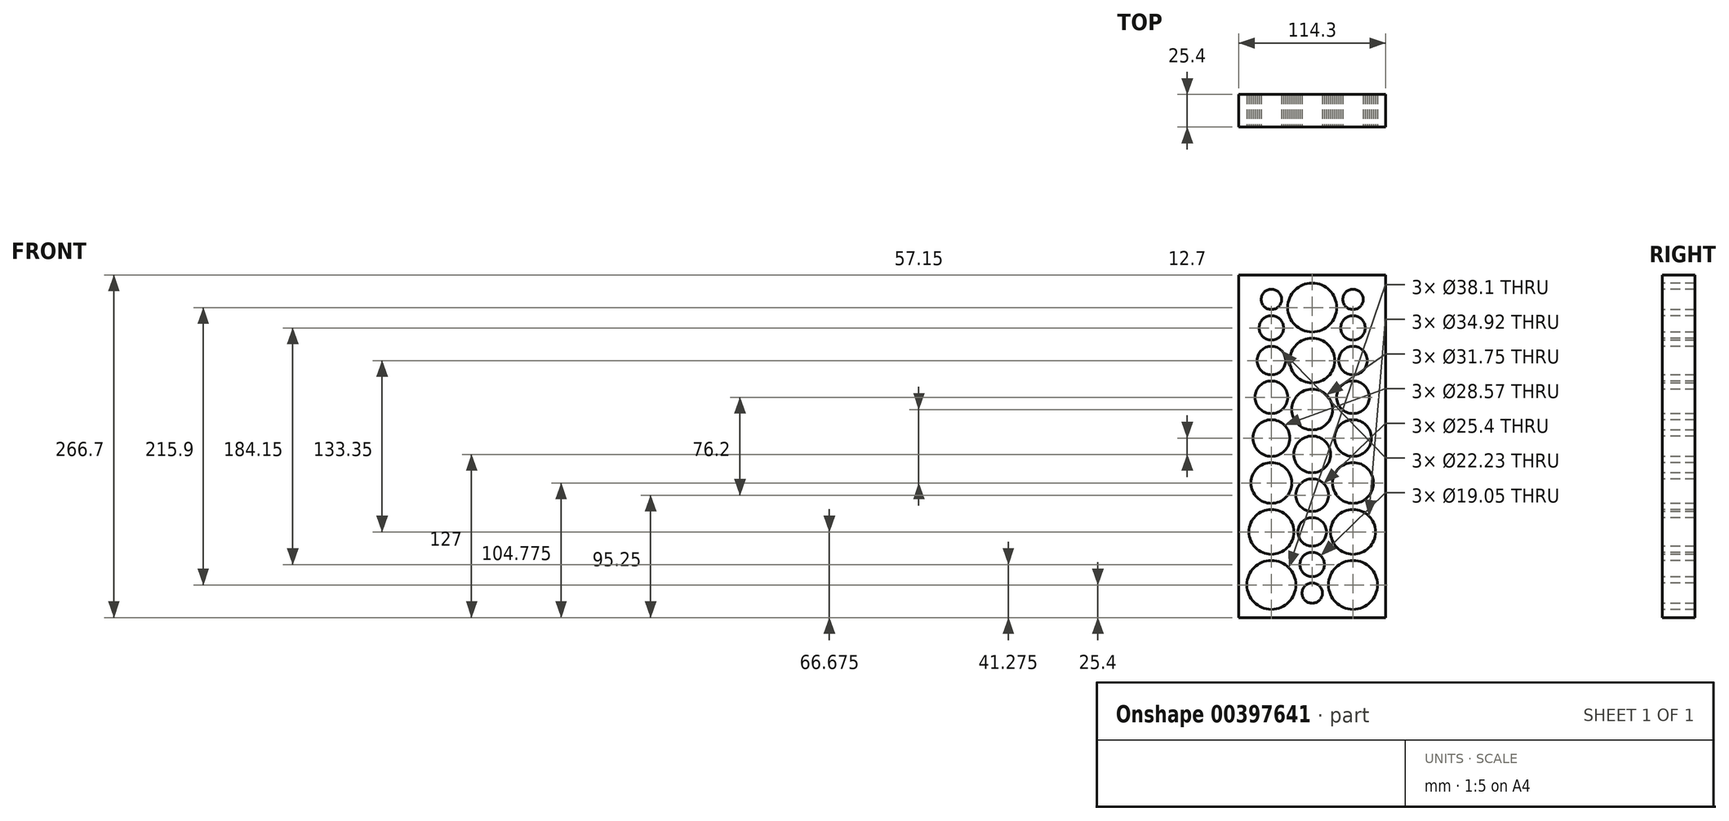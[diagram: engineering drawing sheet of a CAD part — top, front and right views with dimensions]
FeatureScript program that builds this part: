
annotation { "Feature Type Name" : "Feature", "Feature Type Description" : "" }
export const myFeature = defineFeature(function(context is Context, id is Id, definition is map)
    precondition{}
    {
        {
            var Q0;
            Q0=qCreatedBy(makeId("Front.planeOp"),FACE);
            var sketch = newSketch(context, id + "F0", { "sketchPlane" : qUnion([Q0])});
            skLineSegment(sketch, "E0.bottom", {"start": v(0, 0) * mm, "end": v(-114.3, 0) * mm});
            skLineSegment(sketch, "E0.top", {"start": v(0, 266.7) * mm, "end": v(-114.3, 266.7) * mm});
            skLineSegment(sketch, "E0.left", {"start": v(0, 0) * mm, "end": v(0, 266.7) * mm});
            skLineSegment(sketch, "E0.right", {"start": v(-114.3, 0) * mm, "end": v(-114.3, 266.7) * mm});
            skSolve(sketch);
        }
        {
            var Q0;
            Q0 = qSketchRegion(id + "F0", true);
            extrude(context, id + "F1", {"entities" : qUnion([Q0]), "depth" : 25.4 * mm});
        }
        {
            var Q0;
            Q0=makeQuery(id+"F1.opExtrude","CAP_FACE",FACE,{"disambiguationData":[OSD([sQuery(id+"F0.wireOp",EDGE,"E0.bottom"),sQuery(id+"F0.wireOp",EDGE,"E0.top"),sQuery(id+"F0.wireOp",EDGE,"E0.left"),sQuery(id+"F0.wireOp",EDGE,"E0.right")])],"isStart":false});
            var sketch = newSketch(context, id + "F2", { "sketchPlane" : qUnion([Q0])});
            skLineSegment(sketch, "E1", {"start": v(0, 0) * mm, "end": v(-50.8, 0) * mm});
            skLineSegment(sketch, "E2", {"start": v(0, 0) * mm, "end": v(-25.4, 0) * mm});
            skLineSegment(sketch, "E3", {"start": v(-114.3, 0) * mm, "end": v(-63.5, 0) * mm});
            skLineSegment(sketch, "E4", {"start": v(-114.3, 0) * mm, "end": v(-88.9, 0) * mm});
            skLineSegment(sketch, "E5", {"start": v(-25.4, 0) * mm, "end": v(-25.4, 25.4) * mm});
            skCircle(sketch, "E6", {"center": v(-25.4, 25.4) * mm, "radius": 19.05 * mm});
            skLineSegment(sketch, "E7", {"start": v(-25.4, 25.4) * mm, "end": v(-25.4, 66.68) * mm});
            skCircle(sketch, "E8", {"center": v(-25.4, 66.68) * mm, "radius": 17.46 * mm});
            skLineSegment(sketch, "E9", {"start": v(-25.4, 66.68) * mm, "end": v(-25.4, 104.78) * mm});
            skCircle(sketch, "E10", {"center": v(-25.4, 104.78) * mm, "radius": 15.88 * mm});
            skLineSegment(sketch, "E11", {"start": v(-25.4, 104.78) * mm, "end": v(-25.4, 139.7) * mm});
            skCircle(sketch, "E12", {"center": v(-25.4, 139.7) * mm, "radius": 14.29 * mm});
            skLineSegment(sketch, "E13", {"start": v(-25.4, 139.7) * mm, "end": v(-25.4, 171.45) * mm});
            skLineSegment(sketch, "E14", {"start": v(-25.4, 171.45) * mm, "end": v(-25.4, 200.03) * mm});
            skLineSegment(sketch, "E15", {"start": v(-25.4, 200.03) * mm, "end": v(-25.4, 225.43) * mm});
            skLineSegment(sketch, "E16", {"start": v(-25.4, 225.43) * mm, "end": v(-25.4, 247.65) * mm});
            skCircle(sketch, "E17", {"center": v(-25.4, 171.45) * mm, "radius": 12.7 * mm});
            skCircle(sketch, "E18", {"center": v(-25.4, 200.03) * mm, "radius": 11.11 * mm});
            skCircle(sketch, "E19", {"center": v(-25.4, 225.43) * mm, "radius": 9.53 * mm});
            skCircle(sketch, "E20", {"center": v(-25.4, 247.65) * mm, "radius": 7.94 * mm});
            skCircle(sketch, "E21.1.0.0", {"center": v(-88.9, 25.4) * mm, "radius": 19.05 * mm});
            skCircle(sketch, "E21.1.0.1", {"center": v(-88.9, 66.68) * mm, "radius": 17.46 * mm});
            skCircle(sketch, "E21.1.0.2", {"center": v(-88.9, 104.78) * mm, "radius": 15.88 * mm});
            skCircle(sketch, "E21.1.0.3", {"center": v(-88.9, 139.7) * mm, "radius": 14.29 * mm});
            skCircle(sketch, "E21.1.0.4", {"center": v(-88.9, 171.45) * mm, "radius": 12.7 * mm});
            skCircle(sketch, "E21.1.0.5", {"center": v(-88.9, 200.03) * mm, "radius": 11.11 * mm});
            skCircle(sketch, "E21.1.0.6", {"center": v(-88.9, 225.43) * mm, "radius": 9.53 * mm});
            skCircle(sketch, "E21.1.0.7", {"center": v(-88.9, 247.65) * mm, "radius": 7.94 * mm});
            skLineSegment(sketch, "E21.direction1", {"start": v(-25.4, 25.4) * mm, "end": v(-88.9, 25.4) * mm, "construction": true});
            skSolve(sketch);
        }
        {
            var Q0;
            Q0 = qSketchRegion(id + "F2", true);
            extrude(context, id + "F3", {"entities" : qUnion([Q0]), "operationType" : NewBodyOperationType.REMOVE, "oppositeDirection" : true, "depth" : 25.4 * mm});
        }
        {
            var Q0;
            Q0=makeQuery(id+"F1.opExtrude","CAP_FACE",FACE,{"disambiguationData":[OSD([sQuery(id+"F0.wireOp",EDGE,"E0.bottom"),sQuery(id+"F0.wireOp",EDGE,"E0.top"),sQuery(id+"F0.wireOp",EDGE,"E0.left"),sQuery(id+"F0.wireOp",EDGE,"E0.right")])],"isStart":false});
            var sketch = newSketch(context, id + "F4", { "sketchPlane" : qUnion([Q0])});
            skLineSegment(sketch, "E22", {"start": v(0, 0) * mm, "end": v(-57.15, 0) * mm});
            skLineSegment(sketch, "E23", {"start": v(-57.15, 19.05) * mm, "end": v(-57.15, 41.27) * mm});
            skLineSegment(sketch, "E24", {"start": v(-57.15, 41.27) * mm, "end": v(-57.15, 66.67) * mm});
            skLineSegment(sketch, "E25", {"start": v(-57.15, 66.67) * mm, "end": v(-57.15, 95.25) * mm});
            skLineSegment(sketch, "E26", {"start": v(-57.15, 95.25) * mm, "end": v(-57.15, 127) * mm});
            skLineSegment(sketch, "E27", {"start": v(-57.15, 127) * mm, "end": v(-57.15, 161.92) * mm});
            skLineSegment(sketch, "E28", {"start": v(-57.15, 161.92) * mm, "end": v(-57.15, 200.02) * mm});
            skLineSegment(sketch, "E29", {"start": v(-57.15, 200.02) * mm, "end": v(-57.15, 241.3) * mm});
            skLineSegment(sketch, "E30", {"start": v(-57.15, 241.3) * mm, "end": v(-57.15, 266.7) * mm});
            skCircle(sketch, "E31", {"center": v(-57.15, 241.3) * mm, "radius": 19.05 * mm});
            skCircle(sketch, "E32", {"center": v(-57.15, 200.02) * mm, "radius": 17.46 * mm});
            skCircle(sketch, "E33", {"center": v(-57.15, 161.92) * mm, "radius": 15.88 * mm});
            skCircle(sketch, "E34", {"center": v(-57.15, 127) * mm, "radius": 14.29 * mm});
            skCircle(sketch, "E35", {"center": v(-57.15, 95.25) * mm, "radius": 12.7 * mm});
            skCircle(sketch, "E36", {"center": v(-57.15, 66.67) * mm, "radius": 11.11 * mm});
            skCircle(sketch, "E37", {"center": v(-57.15, 41.27) * mm, "radius": 9.53 * mm});
            skCircle(sketch, "E38", {"center": v(-57.15, 19.05) * mm, "radius": 7.94 * mm});
            skSolve(sketch);
        }
        {
            var Q0;
            Q0 = qSketchRegion(id + "F4", true);
            extrude(context, id + "F5", {"entities" : qUnion([Q0]), "operationType" : NewBodyOperationType.REMOVE, "oppositeDirection" : true, "depth" : 25.4 * mm});
        }
    });
